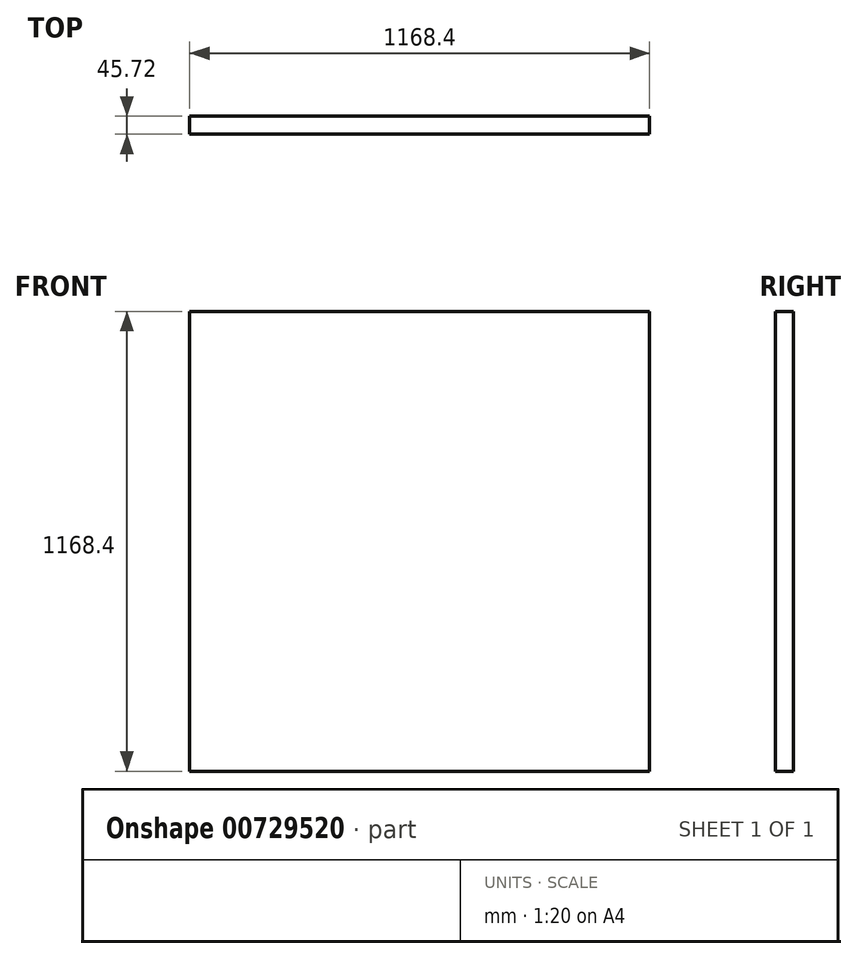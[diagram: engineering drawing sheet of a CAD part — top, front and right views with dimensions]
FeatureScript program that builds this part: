
annotation { "Feature Type Name" : "Feature", "Feature Type Description" : "" }
export const myFeature = defineFeature(function(context is Context, id is Id, definition is map)
    precondition{}
    {
        {
            var Q0;
            Q0=qCreatedBy(makeId("Front.planeOp"),FACE);
            var sketch = newSketch(context, id + "F0", { "sketchPlane" : qUnion([Q0])});
            skLineSegment(sketch, "E0.bottom", {"start": v(-85.42, 1035.6) * mm, "end": v(1082.98, 1035.6) * mm});
            skLineSegment(sketch, "E0.top", {"start": v(-85.42, -132.8) * mm, "end": v(1082.98, -132.8) * mm});
            skLineSegment(sketch, "E0.left", {"start": v(-85.42, 1035.6) * mm, "end": v(-85.42, -132.8) * mm});
            skLineSegment(sketch, "E0.right", {"start": v(1082.98, 1035.6) * mm, "end": v(1082.98, -132.8) * mm});
            skSolve(sketch);
        }
        {
            var Q0;
            Q0 = qSketchRegion(id + "F0", true);
            extrude(context, id + "F1", {"entities" : qUnion([Q0]), "depth" : 45.72 * mm, "offsetDistance" : 25.4 * mm});
        }
    });
